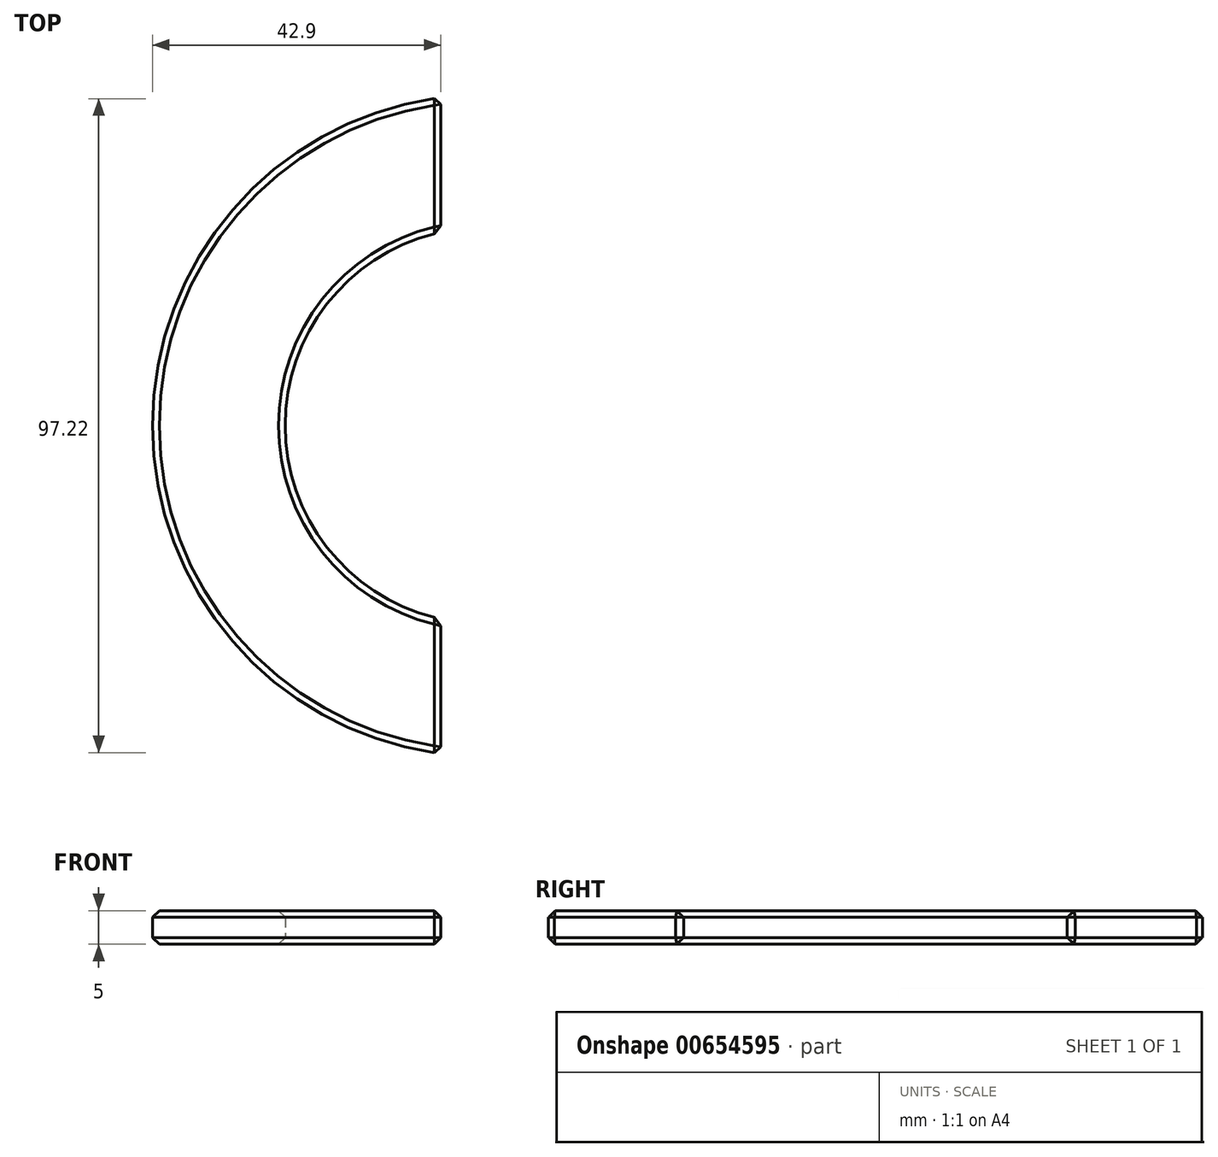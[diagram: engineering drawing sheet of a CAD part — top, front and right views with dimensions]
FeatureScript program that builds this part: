
annotation { "Feature Type Name" : "Feature", "Feature Type Description" : "" }
export const myFeature = defineFeature(function(context is Context, id is Id, definition is map)
    precondition{}
    {
        {
            var Q0;
            Q0=qCreatedBy(makeId("Top.planeOp"),FACE);
            var sketch = newSketch(context, id + "F0", { "sketchPlane" : qUnion([Q0])});
            skArc(sketch, "E0", {"start": v(0, 55) * mm, "mid": v(-42.9, 6.25) * mm, "end": v(0, -42.5) * mm});
            skArc(sketch, "E1", {"start": v(0, 35) * mm, "mid": v(-23.17, 6.25) * mm, "end": v(0, -22.5) * mm});
            skLineSegment(sketch, "E2", {"start": v(0, 55) * mm, "end": v(0, 35) * mm});
            skLineSegment(sketch, "E3", {"start": v(0, -22.5) * mm, "end": v(0, -42.5) * mm});
            skSolve(sketch);
        }
        {
            var Q0;
            Q0=makeQuery(id+"F0.imprint","IMPRINT",FACE,{"disambiguationData":[TD([[makeQuery(id+"F0.imprint","IMPRINT",EDGE,{"derivedFrom":sQuery(id+"F0.wireOp",EDGE,"E0")}),1.0]])]});
            extrude(context, id + "F1", {"entities" : qUnion([Q0]), "depth" : 5 * mm, "offsetDistance" : 25 * mm});
        }
        {
            var Q0;
            Q0=makeQuery(id+"F1.opExtrude","SWEPT_FACE",FACE,{"disambiguationData":[OSD([sQuery(id+"F0.wireOp",EDGE,"E0")])]});
            var Q1;
            Q1=makeQuery(id+"F1.opExtrude","CAP_EDGE",EDGE,{"disambiguationData":[OSD([sQuery(id+"F0.wireOp",EDGE,"E2")])],"isStart":true});
            var Q2;
            Q2=makeQuery(id+"F1.opExtrude","SWEPT_FACE",FACE,{"disambiguationData":[OSD([sQuery(id+"F0.wireOp",EDGE,"E2")])]});
            var Q3;
            Q3=makeQuery(id+"F1.opExtrude","SWEPT_FACE",FACE,{"disambiguationData":[OSD([sQuery(id+"F0.wireOp",EDGE,"E1")])]});
            var Q4;
            Q4=makeQuery(id+"F1.opExtrude","SWEPT_FACE",FACE,{"disambiguationData":[OSD([sQuery(id+"F0.wireOp",EDGE,"E3")])]});
            chamfer(context, id + "F2", {"entities" : qUnion([Q0, Q1, Q2, Q3, Q4]), "width" : 1 * mm, "tangentPropagation" : true});
        }
    });
